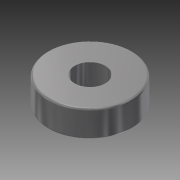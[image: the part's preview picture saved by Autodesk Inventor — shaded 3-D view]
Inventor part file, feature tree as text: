
AUTODESK INVENTOR PART (.ipt)
format: ipt  version: 2015 SP1 (Build 190203100, 203)  size: 102,912 bytes
history: native  units: mm
features: extrude x1, fillet x1, sketch x1
ambient origin geometry x8: Origin, YZ Plane, XZ Plane, XY Plane, X Axis, Y Axis, Z Axis, Center Point
bodies: Solid1 (feature_tree)
feature tree (3):
  extrude  "Extrusion1"  Depth=0.5mm
  fillet  "Fillet1"  Radius=7.0mm
  sketch  "Sketch1"  dims[d0=8.0mm d1=22.0mm d2=7.0mm d3=0.0mm d4=0.5mm]
